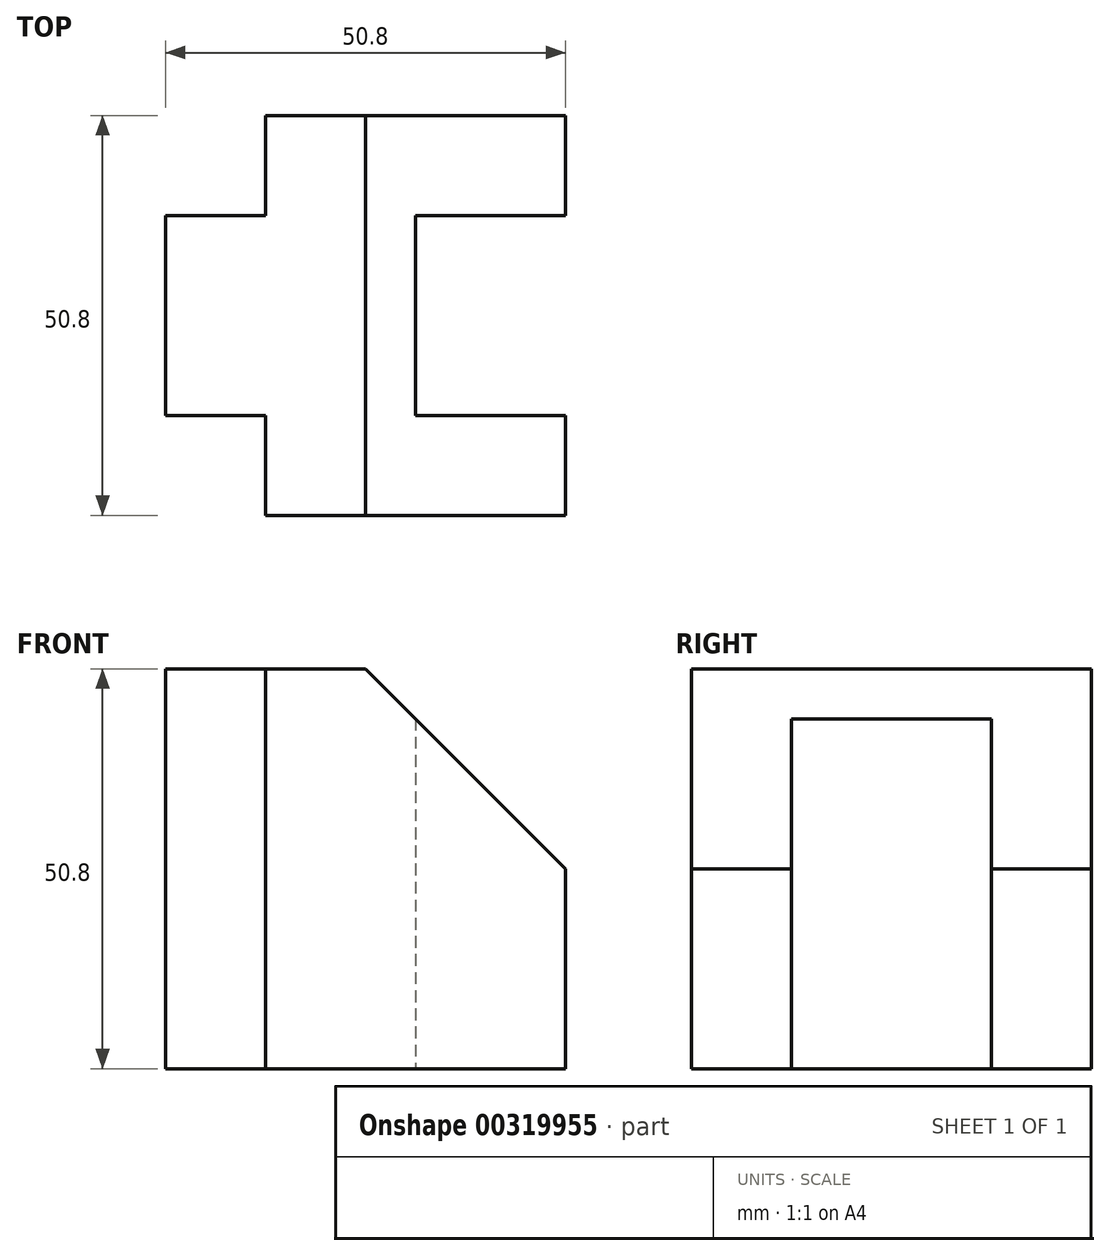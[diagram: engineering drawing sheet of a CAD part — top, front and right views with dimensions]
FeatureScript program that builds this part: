
annotation { "Feature Type Name" : "Feature", "Feature Type Description" : "" }
export const myFeature = defineFeature(function(context is Context, id is Id, definition is map)
    precondition{}
    {
        {
            var Q0;
            Q0=qCreatedBy(makeId("Top.planeOp"),FACE);
            var sketch = newSketch(context, id + "F0", { "sketchPlane" : qUnion([Q0])});
            skLineSegment(sketch, "E0", {"start": v(0, 0) * mm, "end": v(0, 25.4) * mm});
            skLineSegment(sketch, "E1", {"start": v(0, 25.4) * mm, "end": v(12.7, 25.4) * mm});
            skLineSegment(sketch, "E2", {"start": v(0, 0) * mm, "end": v(12.7, 0) * mm});
            skLineSegment(sketch, "E3", {"start": v(12.7, 25.4) * mm, "end": v(12.7, 38.1) * mm});
            skLineSegment(sketch, "E4", {"start": v(12.7, 0) * mm, "end": v(12.7, -12.7) * mm});
            skLineSegment(sketch, "E5", {"start": v(12.7, -12.7) * mm, "end": v(50.8, -12.7) * mm});
            skLineSegment(sketch, "E6", {"start": v(50.8, -12.7) * mm, "end": v(50.8, 0) * mm});
            skLineSegment(sketch, "E7", {"start": v(50.8, 0) * mm, "end": v(31.75, 0) * mm});
            skLineSegment(sketch, "E8", {"start": v(31.75, 25.4) * mm, "end": v(50.8, 25.4) * mm});
            skLineSegment(sketch, "E9", {"start": v(50.8, 25.4) * mm, "end": v(50.8, 38.1) * mm});
            skLineSegment(sketch, "E10", {"start": v(50.8, 38.1) * mm, "end": v(12.7, 38.1) * mm});
            skLineSegment(sketch, "E11", {"start": v(31.75, 25.4) * mm, "end": v(31.75, 0) * mm});
            skSolve(sketch);
        }
        {
            var Q0;
            Q0 = qSketchRegion(id + "F0", true);
            extrude(context, id + "F1", {"entities" : qUnion([Q0]), "endBound" : BoundingType.SYMMETRIC, "depth" : 50.8 * mm});
        }
        {
            var Q0;
            Q0=makeQuery(id+"F1.opExtrude","SWEPT_FACE",FACE,{"disambiguationData":[OSD([sQuery(id+"F0.wireOp",EDGE,"E5")])]});
            var sketch = newSketch(context, id + "F2", { "sketchPlane" : qUnion([Q0])});
            skLineSegment(sketch, "E12", {"start": v(50.8, 0) * mm, "end": v(50.8, 25.4) * mm});
            skLineSegment(sketch, "E13", {"start": v(50.8, 25.4) * mm, "end": v(25.4, 25.4) * mm});
            skLineSegment(sketch, "E14", {"start": v(25.4, 25.4) * mm, "end": v(50.8, 0) * mm});
            skSolve(sketch);
        }
        {
            var Q0;
            Q0 = qSketchRegion(id + "F2", true);
            extrude(context, id + "F3", {"entities" : qUnion([Q0]), "operationType" : NewBodyOperationType.REMOVE, "oppositeDirection" : true, "depth" : 85.85 * mm});
        }
    });
